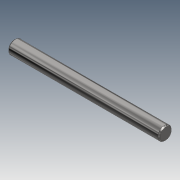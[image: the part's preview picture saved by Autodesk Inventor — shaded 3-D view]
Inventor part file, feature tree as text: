
AUTODESK INVENTOR PART (.ipt)
format: ipt  version: 2017 (Build 210142000, 142)  size: 76,800 bytes
history: native  units: mm
features: other x1, extrude x1, chamfer x1, sketch x1
ambient origin geometry x8: Origin, YZ Plane, XZ Plane, XY Plane, X Axis, Y Axis, Z Axis, Center Point
bodies: Body1 (feature_tree)
feature tree (4):
  other  "Твердое тело1"
  extrude  "Выдавливание1"  Depth=1.2mm
  chamfer  "Фаска1"  Distance=13.5mm
  sketch  "Эскиз1"
